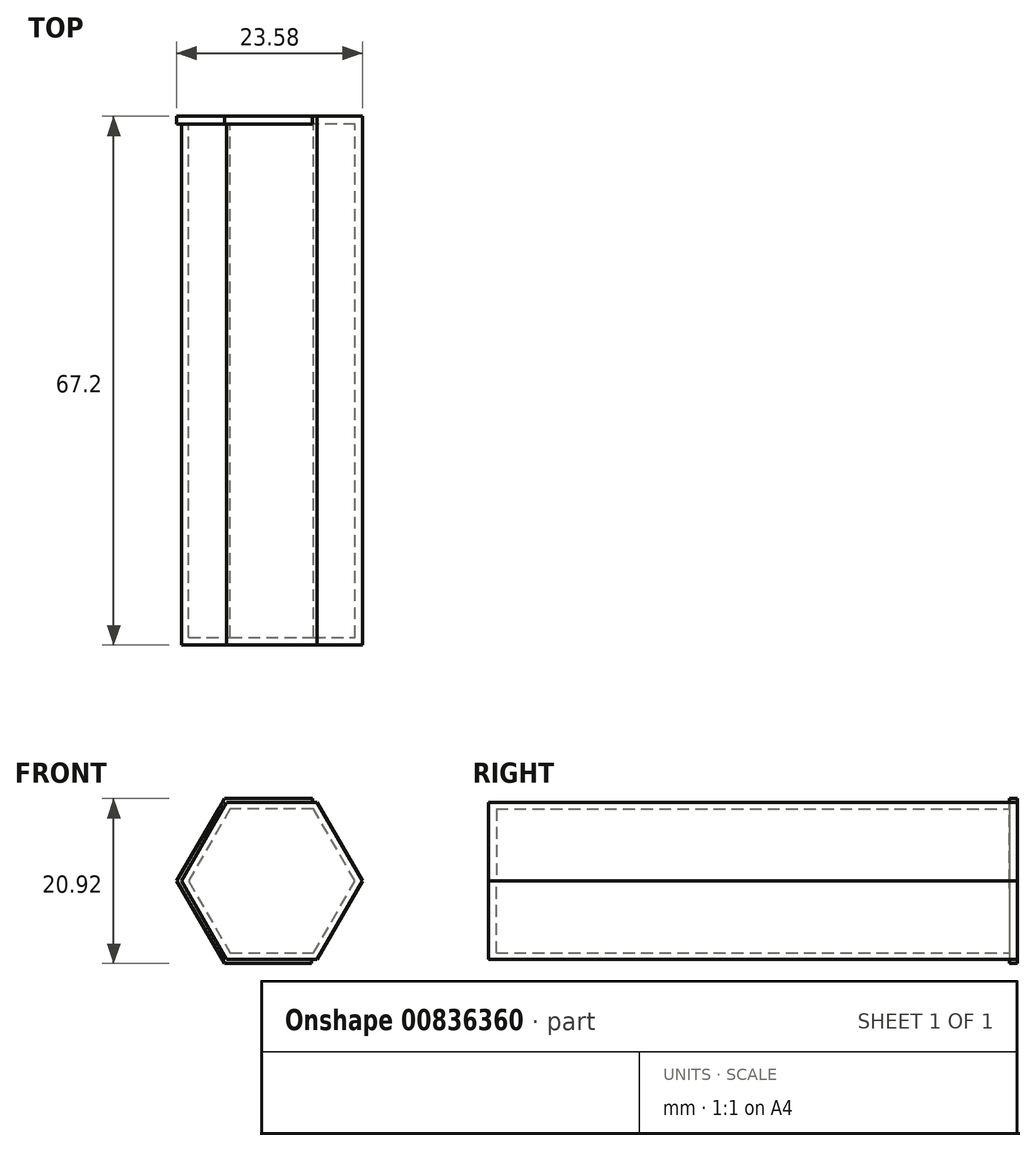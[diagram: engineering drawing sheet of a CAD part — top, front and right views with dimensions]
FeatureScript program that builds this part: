
annotation { "Feature Type Name" : "Feature", "Feature Type Description" : "" }
export const myFeature = defineFeature(function(context is Context, id is Id, definition is map)
    precondition{}
    {
        {
            var Q0;
            Q0=qCreatedBy(makeId("Front.planeOp"),FACE);
            var sketch = newSketch(context, id + "F0", { "sketchPlane" : qUnion([Q0])});
            skLineSegment(sketch, "E0.0", {"start": v(5.75, 9.96) * mm, "end": v(11.5, 0) * mm});
            skLineSegment(sketch, "E0.1", {"start": v(11.5, 0) * mm, "end": v(5.75, -9.96) * mm});
            skLineSegment(sketch, "E0.2", {"start": v(5.75, -9.96) * mm, "end": v(-5.75, -9.96) * mm});
            skLineSegment(sketch, "E0.3", {"start": v(-5.75, -9.96) * mm, "end": v(-11.5, 0) * mm});
            skLineSegment(sketch, "E0.4", {"start": v(-11.5, 0) * mm, "end": v(-5.75, 9.96) * mm});
            skLineSegment(sketch, "E0.5", {"start": v(-5.75, 9.96) * mm, "end": v(5.75, 9.96) * mm});
            skPoint(sketch, "E0.0.midPoint", {"position": v(8.63, 4.98) * mm});
            skSolve(sketch);
        }
        {
            var Q0;
            Q0=makeQuery(id+"F0.imprint","IMPRINT",FACE,{"disambiguationData":[TD([[makeQuery(id+"F0.imprint","IMPRINT",EDGE,{"derivedFrom":sQuery(id+"F0.wireOp",EDGE,"E0.0")}),-1.0]])]});
            extrude(context, id + "F1", {"entities" : qUnion([Q0]), "depth" : 68 * mm, "offsetDistance" : 25 * mm});
        }
        {
            var Q0;
            Q0=makeQuery(id+"F1.opExtrude","CAP_FACE",FACE,{"disambiguationData":[OSD([sQuery(id+"F0.wireOp",EDGE,"E0.0"),sQuery(id+"F0.wireOp",EDGE,"E0.1"),sQuery(id+"F0.wireOp",EDGE,"E0.2"),sQuery(id+"F0.wireOp",EDGE,"E0.3"),sQuery(id+"F0.wireOp",EDGE,"E0.4"),sQuery(id+"F0.wireOp",EDGE,"E0.5")])],"isStart":true});
            shell(context, id + "F2", {"entities" : qUnion([Q0]), "thickness" : .8 * mm});
        }
        {
            var Q0;
            Q0=makeQuery(id+"F1.opExtrude","CAP_FACE",FACE,{"disambiguationData":[OSD([sQuery(id+"F0.wireOp",EDGE,"E0.0"),sQuery(id+"F0.wireOp",EDGE,"E0.1"),sQuery(id+"F0.wireOp",EDGE,"E0.2"),sQuery(id+"F0.wireOp",EDGE,"E0.3"),sQuery(id+"F0.wireOp",EDGE,"E0.4"),sQuery(id+"F0.wireOp",EDGE,"E0.5")])],"isStart":false});
            extrude(context, id + "F3", {"entities" : qUnion([Q0]), "operationType" : NewBodyOperationType.REMOVE, "oppositeDirection" : true, "depth" : .8 * mm, "offsetDistance" : 25 * mm});
        }
        {
            var Q0;
            Q0=makeQuery(id+"F3.boolean.opBoolean","COPY",FACE,{"derivedFrom":makeQuery(id+"F3.opExtrude","CAP_FACE",FACE,{"disambiguationData":[OSD([sQuery(id+"F0.wireOp",EDGE,"E0.0"),sQuery(id+"F0.wireOp",EDGE,"E0.1"),sQuery(id+"F0.wireOp",EDGE,"E0.2"),sQuery(id+"F0.wireOp",EDGE,"E0.3"),sQuery(id+"F0.wireOp",EDGE,"E0.4"),sQuery(id+"F0.wireOp",EDGE,"E0.5")])],"isStart":false})});
            var sketch = newSketch(context, id + "F4", { "sketchPlane" : qUnion([Q0])});
            skLineSegment(sketch, "E1", {"start": v(-10.58, 0) * mm, "end": v(-5.3, -9.16) * mm});
            skLineSegment(sketch, "E2", {"start": v(-5.75, -9.96) * mm, "end": v(-11.5, 0) * mm});
            skLineSegment(sketch, "E3", {"start": v(5.3, 9.16) * mm, "end": v(10.58, 0) * mm});
            skLineSegment(sketch, "E4", {"start": v(11.5, 0) * mm, "end": v(5.75, 9.96) * mm});
            skLineSegment(sketch, "E5", {"start": v(5.75, 9.96) * mm, "end": v(8.63, 4.98) * mm});
            skLineSegment(sketch, "E6", {"start": v(-11.5, 0) * mm, "end": v(-8.63, -4.98) * mm});
            skLineSegment(sketch, "E7", {"start": v(-8.63, -4.98) * mm, "end": v(8.63, 4.98) * mm});
            skLineSegment(sketch, "E8", {"start": v(-10.58, 0) * mm, "end": v(-7.93, -4.58) * mm});
            skLineSegment(sketch, "E9", {"start": v(-7.93, -4.58) * mm, "end": v(7.93, 4.58) * mm});
            skSolve(sketch);
        }
        {
            var Q0;
            Q0=makeQuery(id+"F4.imprint","IMPRINT",FACE,{"disambiguationData":[TD([[makeQuery(id+"F4.imprint","IMPRINT",EDGE,{"derivedFrom":sQuery(id+"F4.wireOp",EDGE,"E8")}),-1.0]])]});
            var sketch = newSketch(context, id + "F5", { "sketchPlane" : qUnion([Q0])});
            skLineSegment(sketch, "E10", {"start": v(-5.29, 9.16) * mm, "end": v(5.3, 9.16) * mm});
            skLineSegment(sketch, "E11", {"start": v(5.3, 9.16) * mm, "end": v(10.58, 0) * mm});
            skLineSegment(sketch, "E12", {"start": v(10.58, 0) * mm, "end": v(5.29, -9.16) * mm});
            skLineSegment(sketch, "E13", {"start": v(5.29, -9.16) * mm, "end": v(-5.3, -9.16) * mm});
            skLineSegment(sketch, "E14", {"start": v(-5.3, -9.16) * mm, "end": v(-10.58, 0) * mm});
            skLineSegment(sketch, "E15", {"start": v(-10.58, 0) * mm, "end": v(-5.29, 9.16) * mm});
            skLineSegment(sketch, "E16", {"start": v(-4.89, 9.16) * mm, "end": v(-4.9, 8.66) * mm});
            skLineSegment(sketch, "E17", {"start": v(4.59, 9.16) * mm, "end": v(4.59, 8.66) * mm});
            skLineSegment(sketch, "E18", {"start": v(5.88, 8.14) * mm, "end": v(5.45, 7.89) * mm});
            skLineSegment(sketch, "E19", {"start": v(9.95, 1.08) * mm, "end": v(9.52, 0.83) * mm});
            skLineSegment(sketch, "E20", {"start": v(10.14, -0.76) * mm, "end": v(9.7, -0.51) * mm});
            skLineSegment(sketch, "E21", {"start": v(5.65, -8.52) * mm, "end": v(5.22, -8.27) * mm});
            skLineSegment(sketch, "E22", {"start": v(4.36, -9.16) * mm, "end": v(4.36, -8.66) * mm});
            skLineSegment(sketch, "E23", {"start": v(-4.58, -9.16) * mm, "end": v(-4.58, -8.66) * mm});
            skLineSegment(sketch, "E24", {"start": v(-6.08, -7.8) * mm, "end": v(-5.65, -7.54) * mm});
            skLineSegment(sketch, "E25", {"start": v(-10.12, -0.79) * mm, "end": v(-9.69, -0.54) * mm});
            skLineSegment(sketch, "E26", {"start": v(-9.76, 1.42) * mm, "end": v(-9.33, 1.17) * mm});
            skLineSegment(sketch, "E27", {"start": v(-5.96, 7.99) * mm, "end": v(-5.53, 7.74) * mm});
            skLineSegment(sketch, "E28", {"start": v(-4.9, 8.66) * mm, "end": v(5.2, 8.66) * mm});
            skLineSegment(sketch, "E29", {"start": v(5.45, 7.89) * mm, "end": v(10.12, -0.2) * mm});
            skLineSegment(sketch, "E30", {"start": v(5.45, 7.89) * mm, "end": v(5, 8.66) * mm});
            skLineSegment(sketch, "E31", {"start": v(9.7, -0.51) * mm, "end": v(10, 0) * mm});
            skLineSegment(sketch, "E32", {"start": v(9.7, -0.51) * mm, "end": v(5.22, -8.27) * mm});
            skLineSegment(sketch, "E33", {"start": v(4.36, -8.66) * mm, "end": v(-4.58, -8.66) * mm});
            skLineSegment(sketch, "E34", {"start": v(-5.65, -7.54) * mm, "end": v(-9.69, -0.54) * mm});
            skLineSegment(sketch, "E35", {"start": v(-9.33, 1.17) * mm, "end": v(-5.53, 7.74) * mm});
            skLineSegment(sketch, "E36", {"start": v(5.22, -8.27) * mm, "end": v(5, -8.66) * mm});
            skLineSegment(sketch, "E37", {"start": v(4.36, -8.66) * mm, "end": v(5, -8.66) * mm});
            skLineSegment(sketch, "E38", {"start": v(-4.58, -8.66) * mm, "end": v(-5.26, -8.66) * mm});
            skLineSegment(sketch, "E39", {"start": v(-5.65, -7.54) * mm, "end": v(-5, -8.66) * mm});
            skLineSegment(sketch, "E40", {"start": v(-9.69, -0.54) * mm, "end": v(-10.16, 0.28) * mm});
            skLineSegment(sketch, "E41", {"start": v(-9.33, 1.17) * mm, "end": v(-10, 0) * mm});
            skLineSegment(sketch, "E42", {"start": v(-5.53, 7.74) * mm, "end": v(-4.97, 8.72) * mm});
            skLineSegment(sketch, "E43", {"start": v(-4.9, 8.66) * mm, "end": v(-5, 8.66) * mm});
            skSolve(sketch);
        }
        {
            var Q0;
            Q0=qSketchRegion(id+"F5",true);
            extrude(context, id + "F6", {"entities" : qUnion([Q0]), "operationType" : NewBodyOperationType.ADD, "oppositeDirection" : true, "depth" : 1 * mm, "offsetDistance" : 25 * mm});
        }
        {
            var Q0;
            Q0=makeQuery(id+"F1.opExtrude","CAP_FACE",FACE,{"disambiguationData":[OSD([sQuery(id+"F0.wireOp",EDGE,"E0.0"),sQuery(id+"F0.wireOp",EDGE,"E0.1"),sQuery(id+"F0.wireOp",EDGE,"E0.2"),sQuery(id+"F0.wireOp",EDGE,"E0.3"),sQuery(id+"F0.wireOp",EDGE,"E0.4"),sQuery(id+"F0.wireOp",EDGE,"E0.5")])],"isStart":true});
            var sketch = newSketch(context, id + "F7", { "sketchPlane" : qUnion([Q0])});
            skLineSegment(sketch, "E44.0", {"start": v(5.75, 9.96) * mm, "end": v(11.5, 0) * mm});
            skLineSegment(sketch, "E44.1", {"start": v(11.5, 0) * mm, "end": v(5.75, -9.96) * mm});
            skLineSegment(sketch, "E44.2", {"start": v(5.75, -9.96) * mm, "end": v(-5.75, -9.96) * mm});
            skLineSegment(sketch, "E44.3", {"start": v(-5.75, -9.96) * mm, "end": v(-11.5, 0) * mm});
            skLineSegment(sketch, "E44.4", {"start": v(-11.5, 0) * mm, "end": v(-5.75, 9.96) * mm});
            skLineSegment(sketch, "E44.5", {"start": v(-5.75, 9.96) * mm, "end": v(5.75, 9.96) * mm});
            skPoint(sketch, "E44.0.midPoint", {"position": v(8.62, 4.98) * mm});
            skLineSegment(sketch, "E45", {"start": v(-5.16, 9.96) * mm, "end": v(-5.16, 10.46) * mm});
            skLineSegment(sketch, "E46", {"start": v(5.13, 9.96) * mm, "end": v(5.13, 10.46) * mm});
            skLineSegment(sketch, "E47", {"start": v(6.3, 8.99) * mm, "end": v(6.74, 9.24) * mm});
            skLineSegment(sketch, "E48", {"start": v(10.97, 0.92) * mm, "end": v(11.4, 1.17) * mm});
            skLineSegment(sketch, "E49", {"start": v(11.08, -0.72) * mm, "end": v(11.52, -0.97) * mm});
            skLineSegment(sketch, "E50", {"start": v(6.31, -8.99) * mm, "end": v(6.74, -9.24) * mm});
            skLineSegment(sketch, "E51", {"start": v(4.73, -9.96) * mm, "end": v(4.73, -10.46) * mm});
            skLineSegment(sketch, "E52", {"start": v(-5.06, -9.96) * mm, "end": v(-5.06, -10.46) * mm});
            skLineSegment(sketch, "E53", {"start": v(-6.37, -8.89) * mm, "end": v(-6.8, -9.14) * mm});
            skLineSegment(sketch, "E54", {"start": v(-11.1, -0.68) * mm, "end": v(-11.54, -0.93) * mm});
            skLineSegment(sketch, "E55", {"start": v(-10.98, 0.9) * mm, "end": v(-11.4, 1.15) * mm});
            skLineSegment(sketch, "E56", {"start": v(-6.19, 9.2) * mm, "end": v(-6.62, 9.45) * mm});
            skLineSegment(sketch, "E57", {"start": v(-5.16, 10.46) * mm, "end": v(7.43, 10.46) * mm});
            skLineSegment(sketch, "E58", {"start": v(6.74, 9.24) * mm, "end": v(6.04, 10.46) * mm});
            skLineSegment(sketch, "E59", {"start": v(6.74, 9.24) * mm, "end": v(13.21, -1.96) * mm});
            skLineSegment(sketch, "E60", {"start": v(11.52, -0.97) * mm, "end": v(5.11, -12.06) * mm});
            skLineSegment(sketch, "E61", {"start": v(4.73, -10.46) * mm, "end": v(6.04, -10.46) * mm});
            skLineSegment(sketch, "E62", {"start": v(4.73, -10.46) * mm, "end": v(-7.08, -10.46) * mm});
            skLineSegment(sketch, "E63", {"start": v(-6.8, -9.14) * mm, "end": v(-6.04, -10.46) * mm});
            skLineSegment(sketch, "E64", {"start": v(-6.8, -9.14) * mm, "end": v(-12.85, 1.33) * mm});
            skLineSegment(sketch, "E65", {"start": v(-11.4, 1.15) * mm, "end": v(-12.08, 0) * mm});
            skLineSegment(sketch, "E66", {"start": v(-11.4, 1.15) * mm, "end": v(-5.5, 11.4) * mm});
            skLineSegment(sketch, "E67", {"start": v(-5.16, 10.46) * mm, "end": v(-6.04, 10.46) * mm});
            skLineSegment(sketch, "E68", {"start": v(11.52, -0.97) * mm, "end": v(12.08, 0) * mm});
            skSolve(sketch);
        }
        {
            var Q0;
            Q0=qSketchRegion(id+"F7",true);
            extrude(context, id + "F8", {"entities" : qUnion([Q0]), "operationType" : NewBodyOperationType.ADD, "oppositeDirection" : true, "depth" : 1 * mm, "offsetDistance" : 25 * mm});
        }
    });
